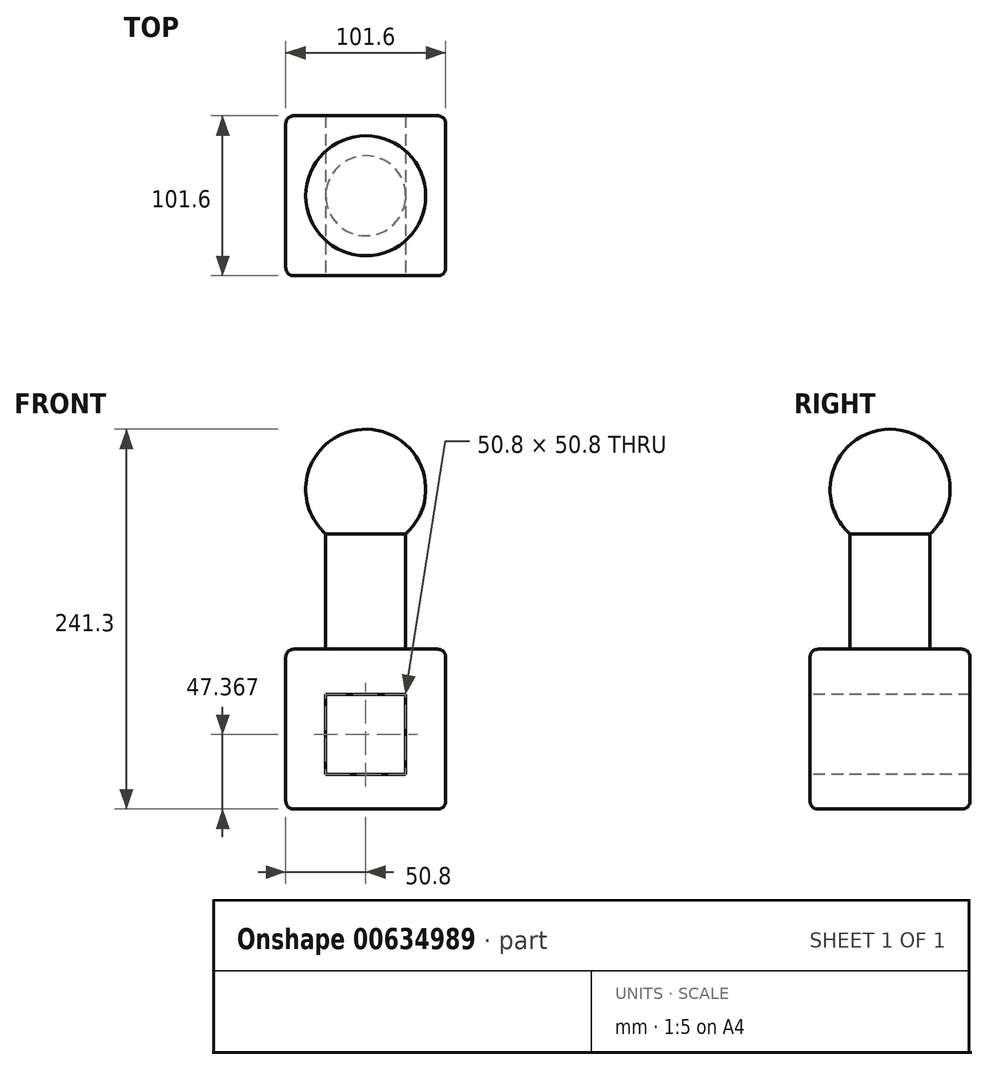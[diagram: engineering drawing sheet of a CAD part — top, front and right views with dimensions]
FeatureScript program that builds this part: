
annotation { "Feature Type Name" : "Feature", "Feature Type Description" : "" }
export const myFeature = defineFeature(function(context is Context, id is Id, definition is map)
    precondition{}
    {
        {
            var Q0;
            Q0=qCreatedBy(makeId("Top.planeOp"),FACE);
            var sketch = newSketch(context, id + "F0", { "sketchPlane" : qUnion([Q0])});
            skLineSegment(sketch, "E0.bottom", {"start": v(50.8, 50.8) * mm, "end": v(-50.8, 50.8) * mm});
            skLineSegment(sketch, "E0.top", {"start": v(50.8, -50.8) * mm, "end": v(-50.8, -50.8) * mm});
            skLineSegment(sketch, "E0.left", {"start": v(50.8, 50.8) * mm, "end": v(50.8, -50.8) * mm});
            skLineSegment(sketch, "E0.right", {"start": v(-50.8, 50.8) * mm, "end": v(-50.8, -50.8) * mm});
            skPoint(sketch, "E0.middle", {"position": v(0, 0) * mm});
            skSolve(sketch);
        }
        {
            var Q0;
            Q0=makeQuery(id+"F0.imprint","IMPRINT",FACE,{"disambiguationData":[TD([[makeQuery(id+"F0.imprint","IMPRINT",EDGE,{"derivedFrom":sQuery(id+"F0.wireOp",EDGE,"E0.bottom")}),1.0]])]});
            extrude(context, id + "F1", {"entities" : qUnion([Q0]), "depth" : 101.6 * mm, "offsetDistance" : 25.4 * mm});
        }
        {
            var Q0;
            Q0=makeQuery(id+"F1.opExtrude","CAP_FACE",FACE,{"disambiguationData":[OSD([sQuery(id+"F0.wireOp",EDGE,"E0.bottom"),sQuery(id+"F0.wireOp",EDGE,"E0.top"),sQuery(id+"F0.wireOp",EDGE,"E0.left"),sQuery(id+"F0.wireOp",EDGE,"E0.right")])],"isStart":false});
            var sketch = newSketch(context, id + "F2", { "sketchPlane" : qUnion([Q0])});
            skCircle(sketch, "E1", {"center": v(0, 0) * mm, "radius": 25.4 * mm});
            skSolve(sketch);
        }
        {
            var Q0;
            Q0 = qSketchRegion(id + "F2", true);
            extrude(context, id + "F3", {"entities" : qUnion([Q0]), "operationType" : NewBodyOperationType.ADD, "depth" : 101.6 * mm, "offsetDistance" : 25.4 * mm});
        }
        {
            var Q0;
            Q0=makeQuery(id+"F3.opExtrude","CAP_FACE",FACE,{"disambiguationData":[OSD([sQuery(id+"F2.wireOp",EDGE,"E1")])],"isStart":false});
            var sketch = newSketch(context, id + "F4", { "sketchPlane" : qUnion([Q0])});
            skArc(sketch, "E2", {"start": v(0, -38.1) * mm, "mid": v(38.1, 0) * mm, "end": v(0, 38.1) * mm});
            skLineSegment(sketch, "E3", {"start": v(0, 38.1) * mm, "end": v(0, -38.1) * mm});
            skSolve(sketch);
        }
        {
            var Q0;
            {var subQ0=sQuery(id+"F4.wireOp",EDGE,"E2");Q0=makeQuery(id+"F4.imprint","IMPRINT",FACE,{"disambiguationData":[TD([[makeQuery(id+"F4.imprint","IMPRINT",EDGE,{"derivedFrom":subQ0}),1.0]])]});}
            var Q1;
            {var subQ0=sQuery(id+"F4.wireOp",EDGE,"E3");var subQ1=makeQuery(id+"F3.opExtrude","CAP_EDGE",EDGE,{"disambiguationData":[OSD([sQuery(id+"F2.wireOp",EDGE,"E1")])],"isStart":false});var subQ2=makeQuery(id+"F4.imprint","INTERSECT",VERTEX,{"disambiguationData":[OD(0.0)],"derivedFrom":[subQ1,subQ0]});Q1=makeQuery(id+"F4.imprint","IMPRINT",FACE,{"disambiguationData":[TD([[makeQuery(id+"F4.imprint","IMPRINT",EDGE,{"disambiguationData":[TD([[subQ2,-1.0]])],"derivedFrom":subQ0}),1.0]])]});}
            var Q2;
            Q2=sQuery(id+"F4.wireOp",EDGE,"E3");
            revolve(context, id + "F5", {"operationType" : NewBodyOperationType.ADD, "surfaceOperationType" : NewSurfaceOperationType.NEW, "entities" : qUnion([Q0, Q1]), "axis" : qUnion([Q2]), "revolveType" : RevolveType.FULL});
        }
        {
            var Q0;
            Q0=makeQuery(id+"F1.opExtrude","SWEPT_FACE",FACE,{"disambiguationData":[OSD([sQuery(id+"F0.wireOp",EDGE,"E0.top")])]});
            var sketch = newSketch(context, id + "F6", { "sketchPlane" : qUnion([Q0])});
            skLineSegment(sketch, "E4.bottom", {"start": v(25.4, 72.77) * mm, "end": v(-25.4, 72.77) * mm});
            skLineSegment(sketch, "E4.top", {"start": v(25.4, 21.97) * mm, "end": v(-25.4, 21.97) * mm});
            skLineSegment(sketch, "E4.left", {"start": v(25.4, 72.77) * mm, "end": v(25.4, 21.97) * mm});
            skLineSegment(sketch, "E4.right", {"start": v(-25.4, 72.77) * mm, "end": v(-25.4, 21.97) * mm});
            skPoint(sketch, "E4.middle", {"position": v(0, 47.37) * mm});
            skLineSegment(sketch, "E5.bottom", {"start": v(25.4, 47.37) * mm, "end": v(25.02, 47.37) * mm});
            skLineSegment(sketch, "E5.top", {"start": v(25.02, 47.37) * mm, "end": v(25.02, 47.37) * mm});
            skLineSegment(sketch, "E5.right", {"start": v(25.02, 47.37) * mm, "end": v(25.02, 47.37) * mm});
            skSolve(sketch);
        }
        {
            var Q0;
            Q0 = qSketchRegion(id + "F6", true);
            extrude(context, id + "F7", {"entities" : qUnion([Q0]), "operationType" : NewBodyOperationType.REMOVE, "oppositeDirection" : true, "depth" : 101.6 * mm, "offsetDistance" : 25.4 * mm});
        }
        {
            var Q0;
            Q0=makeQuery(id+"F1.opExtrude","CAP_EDGE",EDGE,{"disambiguationData":[OSD([sQuery(id+"F0.wireOp",EDGE,"E0.top")])],"isStart":false});
            var Q1;
            Q1=makeQuery(id+"F1.opExtrude","CAP_EDGE",EDGE,{"disambiguationData":[OSD([sQuery(id+"F0.wireOp",EDGE,"E0.left")])],"isStart":false});
            var Q2;
            Q2=makeQuery(id+"F1.opExtrude","CAP_EDGE",EDGE,{"disambiguationData":[OSD([sQuery(id+"F0.wireOp",EDGE,"E0.left")])],"isStart":true});
            var Q3;
            Q3=makeQuery(id+"F1.opExtrude","SWEPT_EDGE",EDGE,{"disambiguationData":[OSD([sQuery(id+"F0.wireOp",EDGE,"E0.top"),sQuery(id+"F0.wireOp",EDGE,"E0.left")])]});
            var Q4;
            Q4=makeQuery(id+"F1.opExtrude","SWEPT_EDGE",EDGE,{"disambiguationData":[OSD([sQuery(id+"F0.wireOp",EDGE,"E0.bottom"),sQuery(id+"F0.wireOp",EDGE,"E0.left")])]});
            var Q5;
            Q5=makeQuery(id+"F1.opExtrude","CAP_EDGE",EDGE,{"disambiguationData":[OSD([sQuery(id+"F0.wireOp",EDGE,"E0.bottom")])],"isStart":false});
            var Q6;
            Q6=makeQuery(id+"F1.opExtrude","CAP_EDGE",EDGE,{"disambiguationData":[OSD([sQuery(id+"F0.wireOp",EDGE,"E0.right")])],"isStart":false});
            var Q7;
            Q7=makeQuery(id+"F3.opExtrude","CAP_EDGE",EDGE,{"disambiguationData":[OSD([sQuery(id+"F2.wireOp",EDGE,"E1")])],"isStart":true});
            fillet(context, id + "F8", {"entities" : qUnion([Q0, Q1, Q2, Q3, Q4, Q5, Q6, Q7]), "radius" : 5.08 * mm, "tangentPropagation" : true, "allowEdgeOverflow" : false});
        }
        {
            var Q0;
            Q0=makeQuery(id+"F1.opExtrude","CAP_EDGE",EDGE,{"disambiguationData":[OSD([sQuery(id+"F0.wireOp",EDGE,"E0.top")])],"isStart":true});
            var Q1;
            {var subQ0=sQuery(id+"F0.wireOp",EDGE,"E0.left");Q1=makeQuery(id+"F8.opFillet","BLEND_EDGE",EDGE,{"blendedFrom":[makeQuery(id+"F1.opExtrude","CAP_EDGE",EDGE,{"disambiguationData":[OSD([subQ0])],"isStart":true}),makeQuery(id+"F1.opExtrude","SWEPT_FACE",FACE,{"disambiguationData":[OSD([subQ0])]})],"blendedInto":[makeQuery(id+"F1.opExtrude","SWEPT_FACE",FACE,{"disambiguationData":[OSD([subQ0])]})]});}
            var Q2;
            Q2=makeQuery(id+"F1.opExtrude","SWEPT_EDGE",EDGE,{"disambiguationData":[OSD([sQuery(id+"F0.wireOp",EDGE,"E0.top"),sQuery(id+"F0.wireOp",EDGE,"E0.right")])]});
            var Q3;
            Q3=makeQuery(id+"F1.opExtrude","CAP_EDGE",EDGE,{"disambiguationData":[OSD([sQuery(id+"F0.wireOp",EDGE,"E0.right")])],"isStart":true});
            var Q4;
            Q4=makeQuery(id+"F1.opExtrude","CAP_EDGE",EDGE,{"disambiguationData":[OSD([sQuery(id+"F0.wireOp",EDGE,"E0.bottom")])],"isStart":true});
            var Q5;
            Q5=makeQuery(id+"F1.opExtrude","SWEPT_EDGE",EDGE,{"disambiguationData":[OSD([sQuery(id+"F0.wireOp",EDGE,"E0.bottom"),sQuery(id+"F0.wireOp",EDGE,"E0.right")])]});
            fillet(context, id + "F9", {"entities" : qUnion([Q0, Q1, Q2, Q3, Q4, Q5]), "radius" : 5.08 * mm, "tangentPropagation" : true, "allowEdgeOverflow" : false});
        }
    });
